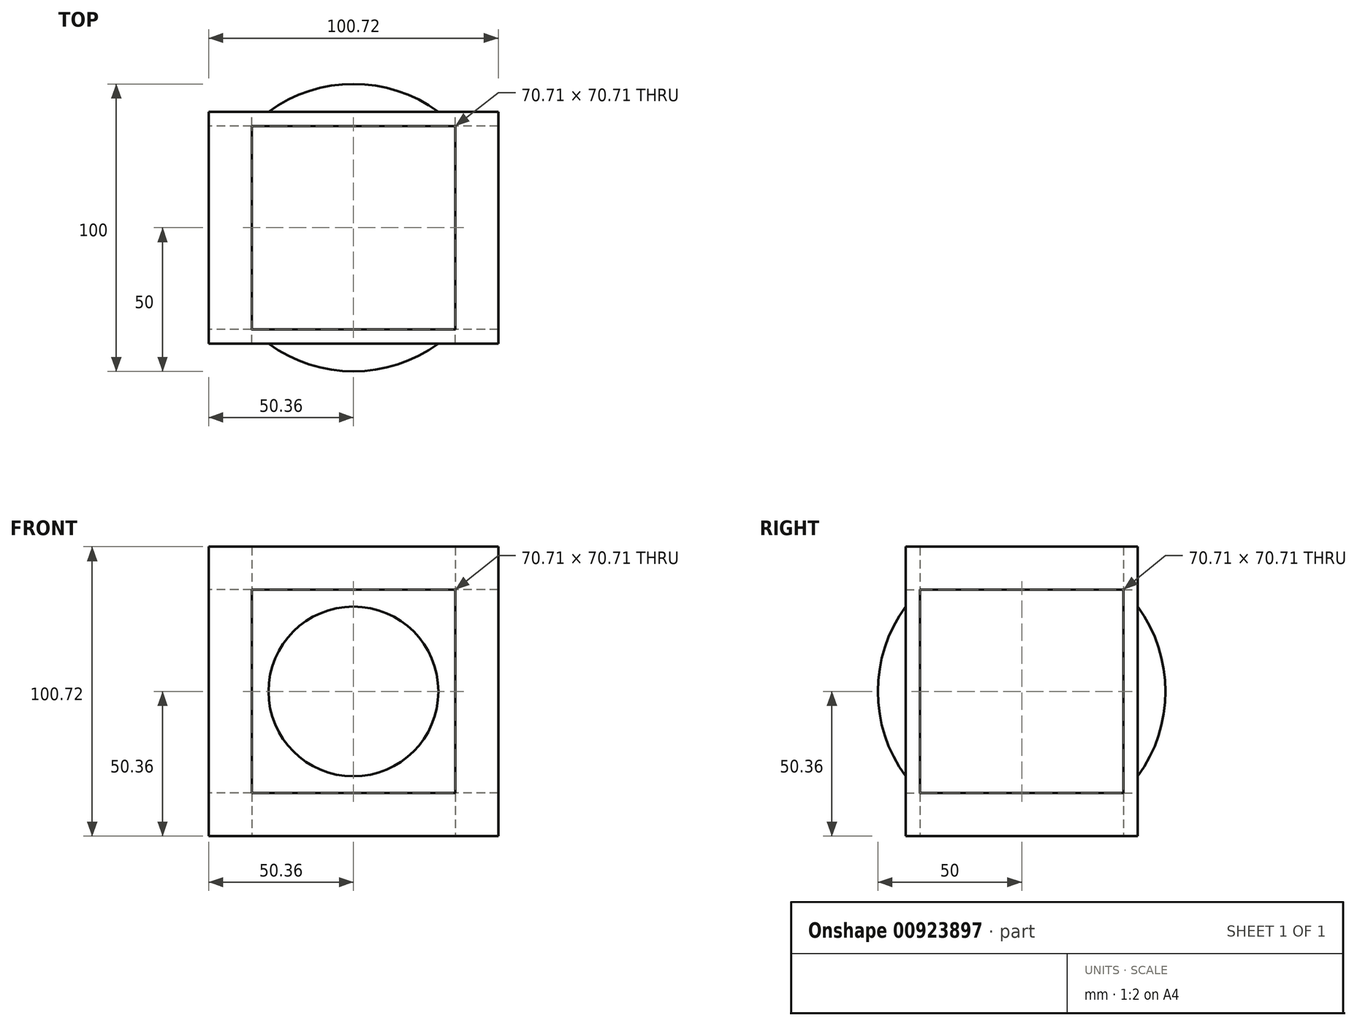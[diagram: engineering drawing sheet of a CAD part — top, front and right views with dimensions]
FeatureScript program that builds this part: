
annotation { "Feature Type Name" : "Feature", "Feature Type Description" : "" }
export const myFeature = defineFeature(function(context is Context, id is Id, definition is map)
    precondition{}
    {
        {
            var Q0;
            Q0=qCreatedBy(makeId("Front.planeOp"),FACE);
            var sketch = newSketch(context, id + "F0", { "sketchPlane" : qUnion([Q0])});
            skCircle(sketch, "E0", {"center": v(0, 0) * mm, "radius": 50 * mm});
            skLineSegment(sketch, "E1.bottom", {"start": v(35.36, 35.36) * mm, "end": v(50.36, 35.36) * mm});
            skLineSegment(sketch, "E1.top", {"start": v(35.36, 50.36) * mm, "end": v(50.36, 50.36) * mm});
            skLineSegment(sketch, "E1.left", {"start": v(35.36, 35.36) * mm, "end": v(35.36, 50.36) * mm});
            skLineSegment(sketch, "E1.right", {"start": v(50.36, 35.36) * mm, "end": v(50.36, 50.36) * mm});
            skLineSegment(sketch, "E2", {"start": v(0, 0) * mm, "end": v(50, 0) * mm, "construction": true});
            skLineSegment(sketch, "E3", {"start": v(0, 0) * mm, "end": v(0, 50) * mm, "construction": true});
            skLineSegment(sketch, "E4.MirrorCS", {"start": v(-35.36, 35.36) * mm, "end": v(-35.36, 50.36) * mm});
            skLineSegment(sketch, "E5.MirrorCS", {"start": v(-50.36, 35.36) * mm, "end": v(-50.36, 50.36) * mm});
            skLineSegment(sketch, "E6.MirrorCS", {"start": v(-35.36, 35.36) * mm, "end": v(-50.36, 35.36) * mm});
            skLineSegment(sketch, "E7.MirrorCS", {"start": v(-35.36, 50.36) * mm, "end": v(-50.36, 50.36) * mm});
            skLineSegment(sketch, "E8.MirrorCS", {"start": v(35.36, -50.36) * mm, "end": v(50.36, -50.36) * mm});
            skLineSegment(sketch, "E9.MirrorCS", {"start": v(35.36, -35.36) * mm, "end": v(50.36, -35.36) * mm});
            skLineSegment(sketch, "E10.MirrorCS", {"start": v(35.36, -35.36) * mm, "end": v(35.36, -50.36) * mm});
            skLineSegment(sketch, "E11.MirrorCS", {"start": v(50.36, -35.36) * mm, "end": v(50.36, -50.36) * mm});
            skLineSegment(sketch, "E12.MirrorCS", {"start": v(-35.36, -35.36) * mm, "end": v(-50.36, -35.36) * mm});
            skLineSegment(sketch, "E13.MirrorCS", {"start": v(-50.36, -35.36) * mm, "end": v(-50.36, -50.36) * mm});
            skLineSegment(sketch, "E14.MirrorCS", {"start": v(-35.36, -35.36) * mm, "end": v(-35.36, -50.36) * mm});
            skLineSegment(sketch, "E15.MirrorCS", {"start": v(-35.36, -50.36) * mm, "end": v(-50.36, -50.36) * mm});
            skLineSegment(sketch, "E16.bottom", {"start": v(-50.36, 50.36) * mm, "end": v(50.36, 50.36) * mm});
            skLineSegment(sketch, "E16.top", {"start": v(-50.36, -50.36) * mm, "end": v(50.36, -50.36) * mm});
            skLineSegment(sketch, "E16.left", {"start": v(-50.36, 50.36) * mm, "end": v(-50.36, -50.36) * mm});
            skLineSegment(sketch, "E16.right", {"start": v(50.36, 50.36) * mm, "end": v(50.36, -50.36) * mm});
            skLineSegment(sketch, "E17.bottom", {"start": v(-35.36, 35.36) * mm, "end": v(35.36, 35.36) * mm});
            skLineSegment(sketch, "E17.top", {"start": v(-35.36, -35.36) * mm, "end": v(35.36, -35.36) * mm});
            skLineSegment(sketch, "E17.left", {"start": v(-35.36, 35.36) * mm, "end": v(-35.36, -35.36) * mm});
            skLineSegment(sketch, "E17.right", {"start": v(35.36, 35.36) * mm, "end": v(35.36, -35.36) * mm});
            skSolve(sketch);
        }
        {
            var Q0;
            Q0=qCreatedBy(makeId("Right.planeOp"),FACE);
            var sketch = newSketch(context, id + "F1", { "sketchPlane" : qUnion([Q0])});
            skCircle(sketch, "E18", {"center": v(0, 0) * mm, "radius": 50 * mm});
            skLineSegment(sketch, "E19.bottom", {"start": v(35.36, 35.36) * mm, "end": v(40.36, 35.36) * mm});
            skLineSegment(sketch, "E19.top", {"start": v(35.36, 40.36) * mm, "end": v(40.36, 40.36) * mm});
            skLineSegment(sketch, "E19.left", {"start": v(35.36, 35.36) * mm, "end": v(35.36, 40.36) * mm});
            skLineSegment(sketch, "E19.right", {"start": v(40.36, 35.36) * mm, "end": v(40.36, 40.36) * mm});
            skLineSegment(sketch, "E20", {"start": v(0, 0) * mm, "end": v(50, 0) * mm, "construction": true});
            skLineSegment(sketch, "E21", {"start": v(0, 0) * mm, "end": v(0, 50) * mm, "construction": true});
            skLineSegment(sketch, "E22.MirrorCS", {"start": v(-35.36, 35.36) * mm, "end": v(-35.36, 40.36) * mm});
            skLineSegment(sketch, "E23.MirrorCS", {"start": v(-40.36, 35.36) * mm, "end": v(-40.36, 40.36) * mm});
            skLineSegment(sketch, "E24.MirrorCS", {"start": v(-35.36, 35.36) * mm, "end": v(-40.36, 35.36) * mm});
            skLineSegment(sketch, "E25.MirrorCS", {"start": v(-35.36, 40.36) * mm, "end": v(-40.36, 40.36) * mm});
            skLineSegment(sketch, "E26.MirrorCS", {"start": v(35.36, -40.36) * mm, "end": v(40.36, -40.36) * mm});
            skLineSegment(sketch, "E27.MirrorCS", {"start": v(35.36, -35.36) * mm, "end": v(40.36, -35.36) * mm});
            skLineSegment(sketch, "E28.MirrorCS", {"start": v(35.36, -35.36) * mm, "end": v(35.36, -40.36) * mm});
            skLineSegment(sketch, "E29.MirrorCS", {"start": v(40.36, -35.36) * mm, "end": v(40.36, -40.36) * mm});
            skLineSegment(sketch, "E30.MirrorCS", {"start": v(-35.36, -35.36) * mm, "end": v(-40.36, -35.36) * mm});
            skLineSegment(sketch, "E31.MirrorCS", {"start": v(-40.36, -35.36) * mm, "end": v(-40.36, -40.36) * mm});
            skLineSegment(sketch, "E32.MirrorCS", {"start": v(-35.36, -35.36) * mm, "end": v(-35.36, -40.36) * mm});
            skLineSegment(sketch, "E33.MirrorCS", {"start": v(-35.36, -40.36) * mm, "end": v(-40.36, -40.36) * mm});
            skLineSegment(sketch, "E34.bottom", {"start": v(-40.36, 40.36) * mm, "end": v(40.36, 40.36) * mm});
            skLineSegment(sketch, "E34.top", {"start": v(-40.36, -40.36) * mm, "end": v(40.36, -40.36) * mm});
            skLineSegment(sketch, "E34.left", {"start": v(-40.36, 40.36) * mm, "end": v(-40.36, -40.36) * mm});
            skLineSegment(sketch, "E34.right", {"start": v(40.36, 40.36) * mm, "end": v(40.36, -40.36) * mm});
            skLineSegment(sketch, "E35.bottom", {"start": v(-35.36, 35.36) * mm, "end": v(35.36, 35.36) * mm});
            skLineSegment(sketch, "E35.top", {"start": v(-35.36, -35.36) * mm, "end": v(35.36, -35.36) * mm});
            skLineSegment(sketch, "E35.left", {"start": v(-35.36, 35.36) * mm, "end": v(-35.36, -35.36) * mm});
            skLineSegment(sketch, "E35.right", {"start": v(35.36, 35.36) * mm, "end": v(35.36, -35.36) * mm});
            skSolve(sketch);
        }
        {
            var Q0;
            Q0=qCreatedBy(makeId("Front.planeOp"),FACE);
            var sketch = newSketch(context, id + "F2", { "sketchPlane" : qUnion([Q0])});
            skArc(sketch, "E36.0", {"start": v(50, 0) * mm, "mid": v(0, 50) * mm, "end": v(-50, 0) * mm});
            skLineSegment(sketch, "E37", {"start": v(0, 0) * mm, "end": v(66.08, 0) * mm, "construction": true});
            skLineSegment(sketch, "E38", {"start": v(-50, 0) * mm, "end": v(50, 0) * mm});
            skPoint(sketch, "E38.startSnap0", {"position": v(33.04, 0) * mm});
            skSolve(sketch);
        }
        {
            var Q0;
            Q0=makeQuery(id+"F2.imprint","IMPRINT",FACE,{"disambiguationData":[TD([[makeQuery(id+"F2.imprint","IMPRINT",EDGE,{"derivedFrom":sQuery(id+"F2.wireOp",EDGE,"E36.0")}),1.0]])]});
            var Q1;
            Q1=sQuery(id+"F2.wireOp",EDGE,"E37");
            revolve(context, id + "F3", {"surfaceOperationType" : NewSurfaceOperationType.NEW, "entities" : qUnion([Q0]), "axis" : qUnion([Q1]), "revolveType" : RevolveType.FULL});
        }
        {
            var Q0;
            Q0=qCreatedBy(makeId("Front.planeOp"),FACE);
            var sketch = newSketch(context, id + "F4", { "sketchPlane" : qUnion([Q0])});
            skLineSegment(sketch, "E39.0", {"start": v(-50.36, 50.36) * mm, "end": v(50.36, 50.36) * mm});
            skLineSegment(sketch, "E39.1", {"start": v(-50.36, 50.36) * mm, "end": v(-50.36, -50.36) * mm});
            skLineSegment(sketch, "E39.2", {"start": v(-50.36, -50.36) * mm, "end": v(50.36, -50.36) * mm});
            skLineSegment(sketch, "E39.3", {"start": v(50.36, 50.36) * mm, "end": v(50.36, -50.36) * mm});
            skSolve(sketch);
        }
        {
            var Q0;
            Q0 = qSketchRegion(id + "F4", true);
            var Q1;
            Q1=sQuery(id+"F1.wireOp",VERTEX,"E23.MirrorCS.end");
            var Q2;
            Q2=sQuery(id+"F1.wireOp",VERTEX,"E19.top.end");
            extrude(context, id + "F5", {"entities" : qUnion([Q0]), "endBound" : BoundingType.UP_TO_VERTEX, "depth" : 25 * mm, "endBoundEntityVertex" : qUnion([Q1]), "offsetDistance" : 25 * mm, "hasSecondDirection" : true, "secondDirectionBound" : BoundingType.UP_TO_VERTEX, "secondDirectionOppositeDirection" : true, "secondDirectionDepth" : 25 * mm, "secondDirectionBoundEntityVertex" : qUnion([Q2])});
        }
        {
            var Q0;
            Q0=makeQuery(id+"F5.opExtrude","SWEPT_FACE",FACE,{"disambiguationData":[OSD([sQuery(id+"F4.wireOp",EDGE,"E39.1")])]});
            var sketch = newSketch(context, id + "F6", { "sketchPlane" : qUnion([Q0])});
            skLineSegment(sketch, "E40.0", {"start": v(35.36, 35.36) * mm, "end": v(-35.36, 35.36) * mm});
            skLineSegment(sketch, "E40.1", {"start": v(-35.36, 35.36) * mm, "end": v(-35.36, -35.36) * mm});
            skLineSegment(sketch, "E40.2", {"start": v(35.36, 35.36) * mm, "end": v(35.36, -35.36) * mm});
            skLineSegment(sketch, "E40.3", {"start": v(35.36, -35.36) * mm, "end": v(-35.36, -35.36) * mm});
            skSolve(sketch);
        }
        {
            var Q0;
            Q0 = qSketchRegion(id + "F6", true);
            extrude(context, id + "F7", {"entities" : qUnion([Q0]), "operationType" : NewBodyOperationType.REMOVE, "endBound" : BoundingType.THROUGH_ALL, "oppositeDirection" : true, "depth" : 25 * mm, "offsetDistance" : 25 * mm});
        }
        {
            var Q0;
            Q0=makeQuery(id+"F5.opExtrude","CAP_FACE",FACE,{"disambiguationData":[OSD([sQuery(id+"F4.wireOp",EDGE,"E39.0"),sQuery(id+"F4.wireOp",EDGE,"E39.1"),sQuery(id+"F4.wireOp",EDGE,"E39.2"),sQuery(id+"F4.wireOp",EDGE,"E39.3")])],"isStart":true});
            var sketch = newSketch(context, id + "F8", { "sketchPlane" : qUnion([Q0])});
            skLineSegment(sketch, "E41.0", {"start": v(35.36, 35.36) * mm, "end": v(-35.36, 35.36) * mm});
            skLineSegment(sketch, "E41.1", {"start": v(35.36, 35.36) * mm, "end": v(35.36, -35.36) * mm});
            skLineSegment(sketch, "E41.2", {"start": v(-35.36, 35.36) * mm, "end": v(-35.36, -35.36) * mm});
            skLineSegment(sketch, "E41.3", {"start": v(35.36, -35.36) * mm, "end": v(-35.36, -35.36) * mm});
            skSolve(sketch);
        }
        {
            var Q0;
            Q0 = qSketchRegion(id + "F8", true);
            var Q1;
            Q1=makeQuery(id+"F5.opExtrude","CAP_FACE",FACE,{"disambiguationData":[OSD([sQuery(id+"F4.wireOp",EDGE,"E39.0"),sQuery(id+"F4.wireOp",EDGE,"E39.1"),sQuery(id+"F4.wireOp",EDGE,"E39.2"),sQuery(id+"F4.wireOp",EDGE,"E39.3")])],"isStart":false});
            extrude(context, id + "F9", {"entities" : qUnion([Q0]), "operationType" : NewBodyOperationType.REMOVE, "endBound" : BoundingType.UP_TO_SURFACE, "oppositeDirection" : true, "depth" : 25 * mm, "endBoundEntityFace" : qUnion([Q1]), "offsetDistance" : 25 * mm});
        }
        {
            var Q0;
            Q0=makeQuery(id+"F5.opExtrude","SWEPT_FACE",FACE,{"disambiguationData":[OSD([sQuery(id+"F4.wireOp",EDGE,"E39.2")])]});
            var sketch = newSketch(context, id + "F10", { "sketchPlane" : qUnion([Q0])});
            skLineSegment(sketch, "E42.bottom", {"start": v(35.36, 35.36) * mm, "end": v(-35.36, 35.36) * mm});
            skLineSegment(sketch, "E42.top", {"start": v(35.36, -35.36) * mm, "end": v(-35.36, -35.36) * mm});
            skLineSegment(sketch, "E42.left", {"start": v(35.36, 35.36) * mm, "end": v(35.36, -35.36) * mm});
            skLineSegment(sketch, "E42.right", {"start": v(-35.36, 35.36) * mm, "end": v(-35.36, -35.36) * mm});
            skSolve(sketch);
        }
        {
            var Q0;
            Q0 = qSketchRegion(id + "F10", true);
            var Q1;
            Q1=makeQuery(id+"F5.opExtrude","SWEPT_FACE",FACE,{"disambiguationData":[OSD([sQuery(id+"F4.wireOp",EDGE,"E39.0")])]});
            extrude(context, id + "F11", {"entities" : qUnion([Q0]), "operationType" : NewBodyOperationType.REMOVE, "endBound" : BoundingType.UP_TO_SURFACE, "oppositeDirection" : true, "depth" : 25 * mm, "endBoundEntityFace" : qUnion([Q1]), "offsetDistance" : 25 * mm});
        }
    });
